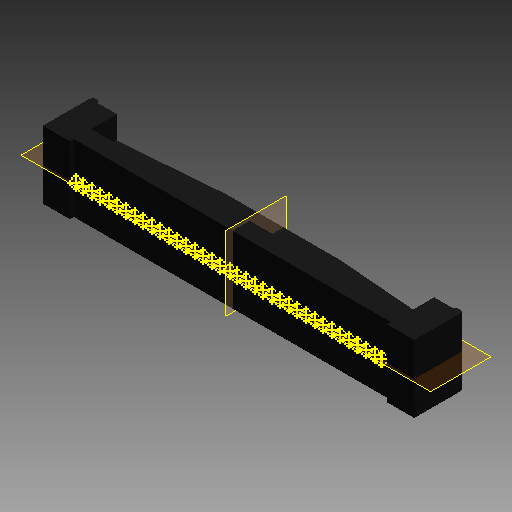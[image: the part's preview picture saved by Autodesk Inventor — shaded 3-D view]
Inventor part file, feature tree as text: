
AUTODESK INVENTOR PART (.ipt)
format: ipt  version: 2019 (Build 230136000, 136)  size: 238,080 bytes
history: native  units: mm (DEFAULTED — no unit token found)
features: sketch x8, extrude x5, fillet x1
ambient origin geometry x8: Origin, YZ Plane, XZ Plane, XY Plane, X Axis, Y Axis, Z Axis, Center Point
bodies: Solid1 (feature_tree)
feature tree (14):
  extrude  "Extrusion1"  Depth=10.0mm
  extrude  "Extrusion2"  Depth=47.0mm
  extrude  "Extrusion3"  Depth=7.4676mm TaperAngle=0.0deg
  extrude  "Extrusion4"  Depth=2.54mm
  extrude  "Extrusion5"  Depth=1.3208mm
  fillet  "Fillet1"  Radius=0.762mm
  sketch  "Sketch8"  dims[d15=8.128mm]
  sketch  "Sketch9"  dims[d16=16.891mm]
  sketch  "Sketch11"  dims[d17=0.508mm d18=3.302mm d19=0.0mm d20=1.143mm d21=3.302mm d22=0.0mm d23=0.5842mm d37=0.508mm d38=0.5842mm d39=0.254mm d40=160.0mm d42=1.27mm d43=10.0mm d45=25.4mm d48=1.27mm d49=1.27mm d50=1.27mm d51=1.27mm d53=1.27mm d54=1.27mm d55=1.27mm d56=1.27mm d57=1.27mm d58=1.27mm d59=1.27mm d60=1.27mm d61=1.27mm d62=1.27mm d64=0.4318mm d65=2.032mm d66=1.27mm d67=0.4318mm d68=0.4318mm d69=1.27mm d70=20.0mm d72=22.86mm d73=10.0mm d75=25.4mm d77=20.0mm d79=1.3843mm d80=10.0mm d82=25.4mm d84=20.0mm d86=1.016mm d87=10.0mm d89=25.4mm d91=20.0mm d93=1.016mm d94=10.0mm d96=25.4mm]
  sketch  "Sketch1"  dims[d0=55.0mm d1=10.0mm]
  sketch  "Sketch2"  dims[d2=7.4676mm d3=0.0mm d4=47.0mm]
  sketch  "Sketch3"  dims[d5=0.5842mm d6=7.4676mm d7=0.0mm]
  sketch  "Sketch4"  dims[d8=47.0mm d9=2.54mm]
  sketch  "Sketch5"  dims[d11=7.4676mm d12=0.0mm d13=1.3208mm d14=0.762mm]
